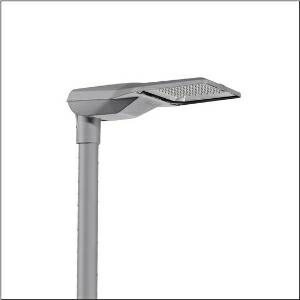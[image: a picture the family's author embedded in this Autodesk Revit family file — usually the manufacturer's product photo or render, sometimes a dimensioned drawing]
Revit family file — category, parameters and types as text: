
# Revit family: streetlight_sl_21_iq_midi___st0_8a_5xe3c31g08mb_0ba1
name_source: partatom
category: Lighting Fixtures
units: mm (PartAtom-declared; Revit-internal decimal feet)

## family parameters
Cut with Voids When Loaded = No
Host = Face
Light Source = No
Part Type = Normal
Room Calculation Point = No
Round Connector Dimension = Use Diameter
Shared = No

## types (1)
- --- (1 x LED, 19500 lm, 146.7 W, 3000K)
    Apparent Load = 147 VA
    CIE Flux Codes = 38 75 97 100 100
    Color Rendering = 70
    Color Temperature = 3000K
    Default Elevation = 1800 mm
    Description = Streetlight SL 21 iQ midi, mast luminaire, primary light control with lens, of PMMA, primary optical cover: cover, of toughened safety glass, transparent, light distribution: ST0.8a, light emission: direct distribution, primary light characteristic: asymmetric, installation type: post-top, side-entry, LED, High Power LED, rated luminous flux: 19.500lm, luminous efficacy: 133lm/W, light colour: 730, colour temperature: 3000K, control gear: iQ Street-Remote, control: Street-Remote, Auto-Match, Temp-Guard, Lumen-Switch, Night-Set, Smart-Wire, Light-Fading, Desk-Remote (wireless, voltage-free reading and setting of iQ features in the workshop via application-optimized NFC function/RFID function), optimised constant luminous flux control (CLO 2.0), pre-setting: linear dimming characteristic, mains connection: 230..240V, AC, 50/60Hz, start of lifetime: 147W, end of service life: 161W, reduction: 62W, luminaire housing, of diecast aluminium, powder-coated, SITECO metallic grey (DB 702S), corrosivity category C5 high according to DIN EN ISO 12944, please order mast flange separately, inclination adjustable: 0°, 5°, 10°, 15°, sealing non-destructively replaceable, multi-level sealing system, length: 644mm, width: 335mm, height: 110mm, mast flange for spigot size: 42mm (side-entry): 5XC10008XM4, 60/48mm (side-entry/post-top): 5XC10108XM2, 76/60mm (side-entry/post-top): 5XC10108XM1, mounting height: 4..8m, protection rating (complete): IP66, insulation class (complete): insulation class II (safety insulation), certification: CE, ENEC, ENEC+, VDE, impact resistance: IK10, permissible operating ambient temperature for outdoor applications: -40..+50°C, standard-compliant lighting for roads and squares, packaging unit: 1 piece

Light Distribution: ST0.8a
    Height = 111 mm
    Lamp = 1 x LED
    Lamp Light Flux = 19500 lm
    Lamp Power = 146.7 W
    Lamp count = 1
    Length = 644 mm
    Luminous efficacy = 133 lm/W
    Manufacturer = Siteco
    ModVariant = No
    Model = 5XE3C31G08MB
    Number of Poles = 1
    OnlyDefault = Yes
    Power Factor = 1
    Product Name = Streetlight SL 21 iQ midi | ST0.8a
    Product group = mast luminaire | pylon top
    ProductGroupID = 6100
    Protection Class = Protection class II
    Protection Degree = IP 66
    RLX_Detail_Level = 1
    RLX_Emergency_Light_Flux = 0 lm
    RLX_Emergency_Type = 0
    RLX_Emergency_Type_DB = No
    RlxData = <blob elided: 26965 chars, md5=e1fd3644>
    Socket = socket
    Standby Power = 0 W
    System Light Flux = 19499 lm
    System Power = 147 W
    Type Comments = factory setting: luminous flux: 100 % | dim-lin: 254 | 753 mA
    Type Image = l_1004298.jpg
    URL = http://relux.com
    VarID = @adj_183683
    Voltage = 0 V
    Weight = 0.00 kg
    Width = 336 mm

## geometry (parser evidence)
native form markers: Blend x4, Sweep x10
no freeform markers — native parametric forms only
